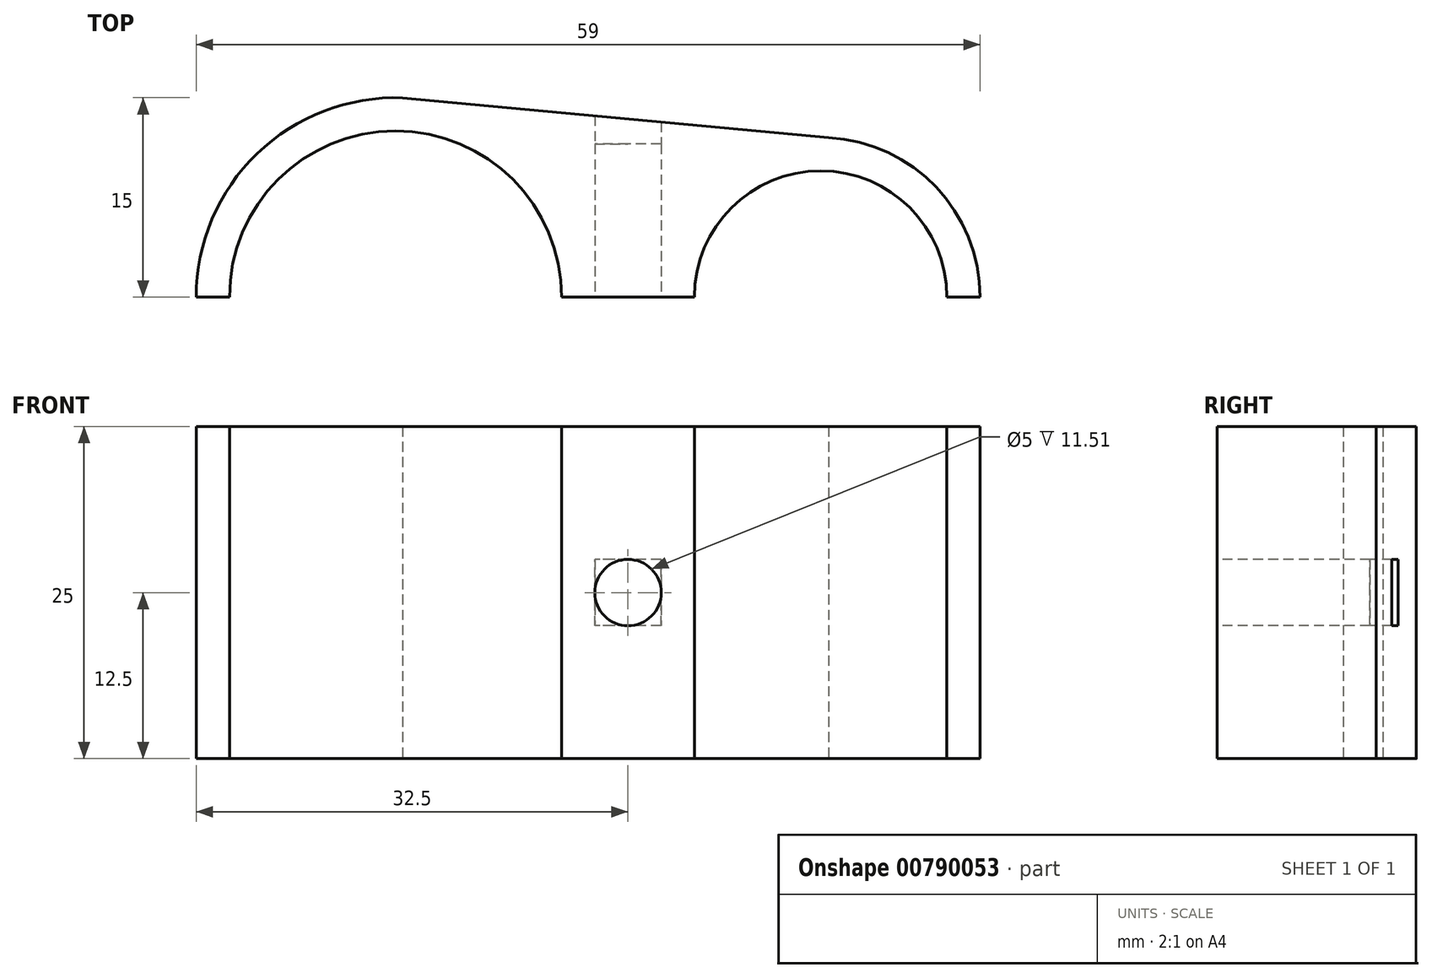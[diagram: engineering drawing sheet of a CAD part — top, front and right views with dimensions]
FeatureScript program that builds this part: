
annotation { "Feature Type Name" : "Feature", "Feature Type Description" : "" }
export const myFeature = defineFeature(function(context is Context, id is Id, definition is map)
    precondition{}
    {
        {
            var Q0;
            Q0=qCreatedBy(makeId("Top.planeOp"),FACE);
            var sketch = newSketch(context, id + "F0", { "sketchPlane" : qUnion([Q0])});
            skArc(sketch, "E0", {"start": v(-15.23, 14.83) * mm, "mid": v(-32.5, -0.43) * mm, "end": v(-14.37, -14.67) * mm});
            skArc(sketch, "E1", {"start": v(14.78, -12) * mm, "mid": v(26.5, -0.16) * mm, "end": v(15.1, 11.98) * mm});
            skLineSegment(sketch, "E2", {"start": v(15.1, 11.98) * mm, "end": v(-16.98, 15) * mm});
            skLineSegment(sketch, "E3", {"start": v(-17.9, -15) * mm, "end": v(14.78, -12) * mm});
            skCircle(sketch, "E4", {"center": v(-17.5, 0) * mm, "radius": 12.5 * mm});
            skCircle(sketch, "E5", {"center": v(14.5, 0) * mm, "radius": 9.5 * mm});
            skSolve(sketch);
        }
        {
            var Q0;
            {var subQ4=sQuery(id+"F0.wireOp",EDGE,"E1");Q0=makeQuery(id+"F0.imprint","IMPRINT",FACE,{"disambiguationData":[TD([[makeQuery(id+"F0.imprint","IMPRINT",EDGE,{"derivedFrom":subQ4}),1.0]])]});}
            extrude(context, id + "F1", {"entities" : qUnion([Q0]), "depth" : 25 * mm, "offsetDistance" : 25 * mm});
        }
        {
            var Q0;
            Q0=qCreatedBy(makeId("Top.planeOp"),FACE);
            var sketch = newSketch(context, id + "F2", { "sketchPlane" : qUnion([Q0])});
            skLineSegment(sketch, "E6.bottom", {"start": v(-36.24, 0) * mm, "end": v(32.6, 0) * mm});
            skLineSegment(sketch, "E6.top", {"start": v(-36.24, -15.53) * mm, "end": v(32.6, -15.53) * mm});
            skLineSegment(sketch, "E6.left", {"start": v(-36.24, 0) * mm, "end": v(-36.24, -15.53) * mm});
            skLineSegment(sketch, "E6.right", {"start": v(32.6, 0) * mm, "end": v(32.6, -15.53) * mm});
            skSolve(sketch);
        }
        {
            var Q0;
            Q0=makeQuery(id+"F2.imprint","IMPRINT",FACE,{"disambiguationData":[TD([[makeQuery(id+"F2.imprint","IMPRINT",EDGE,{"derivedFrom":sQuery(id+"F2.wireOp",EDGE,"E6.bottom")}),-1.0]])]});
            extrude(context, id + "F3", {"entities" : qUnion([Q0]), "operationType" : NewBodyOperationType.REMOVE, "depth" : 25 * mm, "offsetDistance" : 25 * mm});
        }
        {
            var Q0;
            {var subQ0=sQuery(id+"F0.wireOp",EDGE,"E5");var subQ1=sQuery(id+"F0.wireOp",EDGE,"E4");var subQ2=sQuery(id+"F0.wireOp",EDGE,"E3");var subQ3=sQuery(id+"F0.wireOp",EDGE,"E2");var subQ4=sQuery(id+"F0.wireOp",EDGE,"E1");var subQ5=sQuery(id+"F0.wireOp",EDGE,"E0");Q0=makeQuery(id+"F3.boolean.opBoolean","COPY",FACE,{"disambiguationData":[TD([makeQuery(id+"F1.opExtrude","CAP_FACE",FACE,{"disambiguationData":[OSD([subQ5,subQ4,subQ3,subQ2,subQ1,subQ0])],"isStart":true}),makeQuery(id+"F1.opExtrude","CAP_FACE",FACE,{"disambiguationData":[OSD([subQ5,subQ4,subQ3,subQ2,subQ1,subQ0])],"isStart":false}),makeQuery(id+"F1.opExtrude","SWEPT_FACE",FACE,{"disambiguationData":[OSD([subQ1])]}),makeQuery(id+"F1.opExtrude","SWEPT_FACE",FACE,{"disambiguationData":[OSD([subQ0])]})])],"derivedFrom":makeQuery(id+"F3.opExtrude","SWEPT_FACE",FACE,{"disambiguationData":[OSD([sQuery(id+"F2.wireOp",EDGE,"E6.bottom")])]})});}
            var sketch = newSketch(context, id + "F4", { "sketchPlane" : qUnion([Q0])});
            skCircle(sketch, "E7", {"center": v(0, 12.5) * mm, "radius": 2.5 * mm});
            skSolve(sketch);
        }
        {
            var Q0;
            Q0=makeQuery(id+"F4.imprint","IMPRINT",FACE,{"disambiguationData":[TD([[makeQuery(id+"F4.imprint","IMPRINT",EDGE,{"derivedFrom":sQuery(id+"F4.wireOp",EDGE,"E7")}),1.0]])]});
            extrude(context, id + "F5", {"entities" : qUnion([Q0]), "operationType" : NewBodyOperationType.REMOVE, "oppositeDirection" : true, "depth" : 25 * mm, "offsetDistance" : 25 * mm});
        }
        {
            var Q0;
            Q0=makeQuery(id+"F1.opExtrude","CAP_FACE",FACE,{"disambiguationData":[OSD([sQuery(id+"F0.wireOp",EDGE,"E0"),sQuery(id+"F0.wireOp",EDGE,"E1"),sQuery(id+"F0.wireOp",EDGE,"E2"),sQuery(id+"F0.wireOp",EDGE,"E3"),sQuery(id+"F0.wireOp",EDGE,"E4"),sQuery(id+"F0.wireOp",EDGE,"E5")])],"isStart":false});
            cPlane(context, id + "F6", {"entities" : qUnion([Q0]), "cplaneType" : CPlaneType.OFFSET, "offset" : 12.5 * mm, "oppositeDirection" : true, "width" : 150 * mm, "height" : 150 * mm});
        }
        {
            var Q0;
            Q0=qCreatedBy(id+"F6.planeOp",FACE);
            var sketch = newSketch(context, id + "F7", { "sketchPlane" : qUnion([Q0])});
            skLineSegment(sketch, "E8.bottom", {"start": v(2.5, 13.93) * mm, "end": v(-2.5, 13.93) * mm});
            skLineSegment(sketch, "E8.top", {"start": v(2.5, 11.5) * mm, "end": v(-2.5, 11.5) * mm});
            skLineSegment(sketch, "E8.left", {"start": v(2.5, 13.93) * mm, "end": v(2.5, 11.5) * mm});
            skLineSegment(sketch, "E8.right", {"start": v(-2.5, 13.93) * mm, "end": v(-2.5, 11.5) * mm});
            skSolve(sketch);
        }
        {
            var Q0;
            Q0=makeQuery(id+"F7.imprint","IMPRINT",FACE,{"disambiguationData":[TD([[makeQuery(id+"F7.imprint","IMPRINT",EDGE,{"derivedFrom":sQuery(id+"F7.wireOp",EDGE,"E8.bottom")}),1.0]])]});
            extrude(context, id + "F8", {"entities" : qUnion([Q0]), "operationType" : NewBodyOperationType.REMOVE, "endBound" : BoundingType.SYMMETRIC, "oppositeDirection" : true, "depth" : 5 * mm, "offsetDistance" : 25 * mm});
        }
    });
